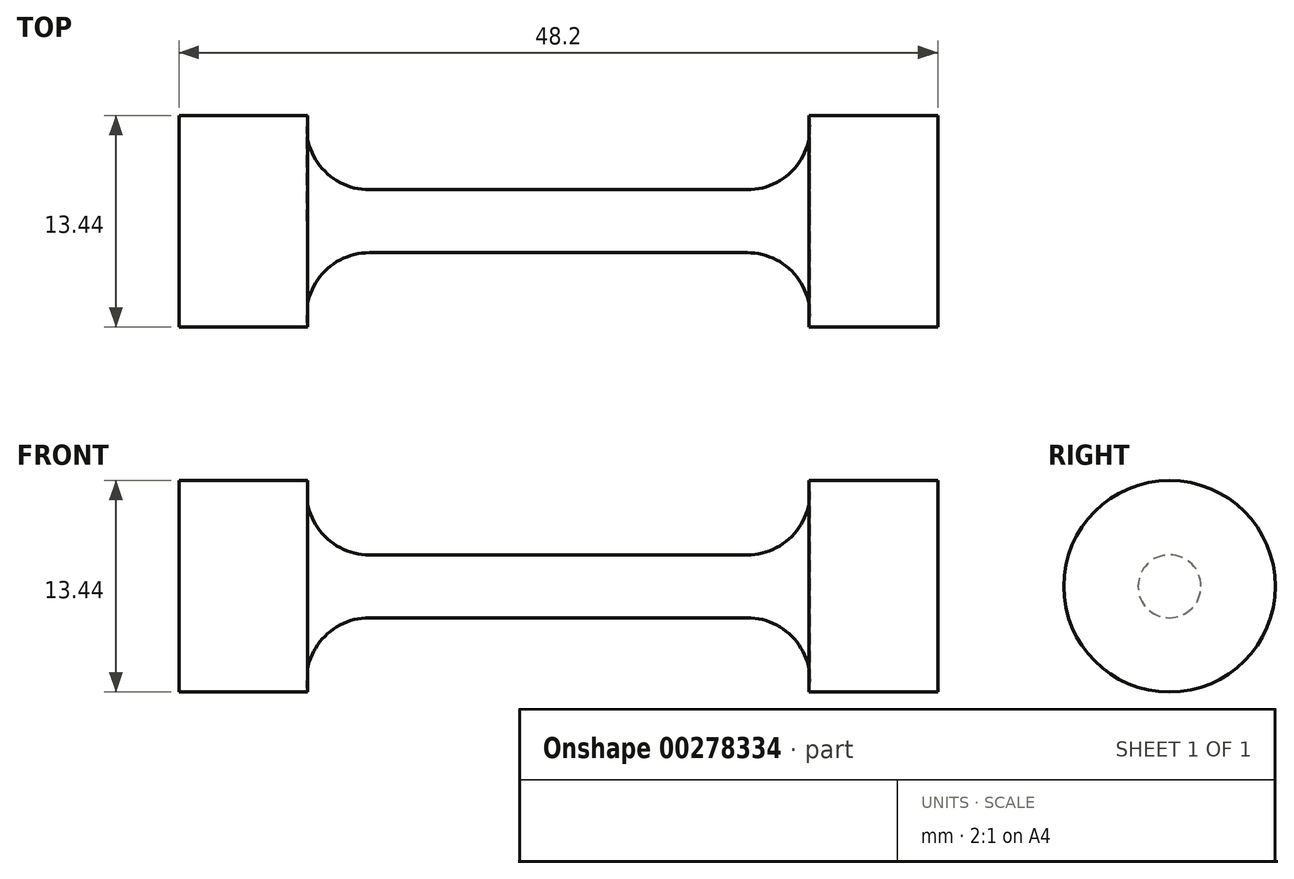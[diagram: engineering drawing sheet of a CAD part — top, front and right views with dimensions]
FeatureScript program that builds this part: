
annotation { "Feature Type Name" : "Feature", "Feature Type Description" : "" }
export const myFeature = defineFeature(function(context is Context, id is Id, definition is map)
    precondition{}
    {
        {
            var Q0;
            Q0=qCreatedBy(makeId("Front.planeOp"),FACE);
            var sketch = newSketch(context, id + "F0", { "sketchPlane" : qUnion([Q0])});
            skLineSegment(sketch, "E0", {"start": v(0, 2) * mm, "end": v(12, 2) * mm});
            skArc(sketch, "E1", {"start": v(12, 2) * mm, "mid": v(15.07, 3.44) * mm, "end": v(15.93, 6.72) * mm});
            skLineSegment(sketch, "E2", {"start": v(15.93, 6.72) * mm, "end": v(24.1, 6.72) * mm});
            skLineSegment(sketch, "E3", {"start": v(24.1, 6.72) * mm, "end": v(24.1, 0) * mm});
            skLineSegment(sketch, "E4.MirrorCS", {"start": v(0, 2) * mm, "end": v(-12, 2) * mm});
            skLineSegment(sketch, "E5.MirrorCS", {"start": v(-24.1, 6.72) * mm, "end": v(-24.1, 0) * mm});
            skLineSegment(sketch, "E6.MirrorCS", {"start": v(-15.93, 6.72) * mm, "end": v(-24.1, 6.72) * mm});
            skArc(sketch, "E7.MirrorCS", {"start": v(-12, 2) * mm, "mid": v(-15.07, 3.44) * mm, "end": v(-15.93, 6.72) * mm});
            skLineSegment(sketch, "E8", {"start": v(-24.1, 0) * mm, "end": v(24.1, 0) * mm});
            skSolve(sketch);
        }
        {
            var Q0;
            Q0 = qSketchRegion(id + "F0", true);
            var Q1;
            Q1=sQuery(id+"F0.wireOp",EDGE,"E8");
            revolve(context, id + "F1", {"entities" : qUnion([Q0]), "axis" : qUnion([Q1]), "revolveType" : RevolveType.FULL});
        }
    });
